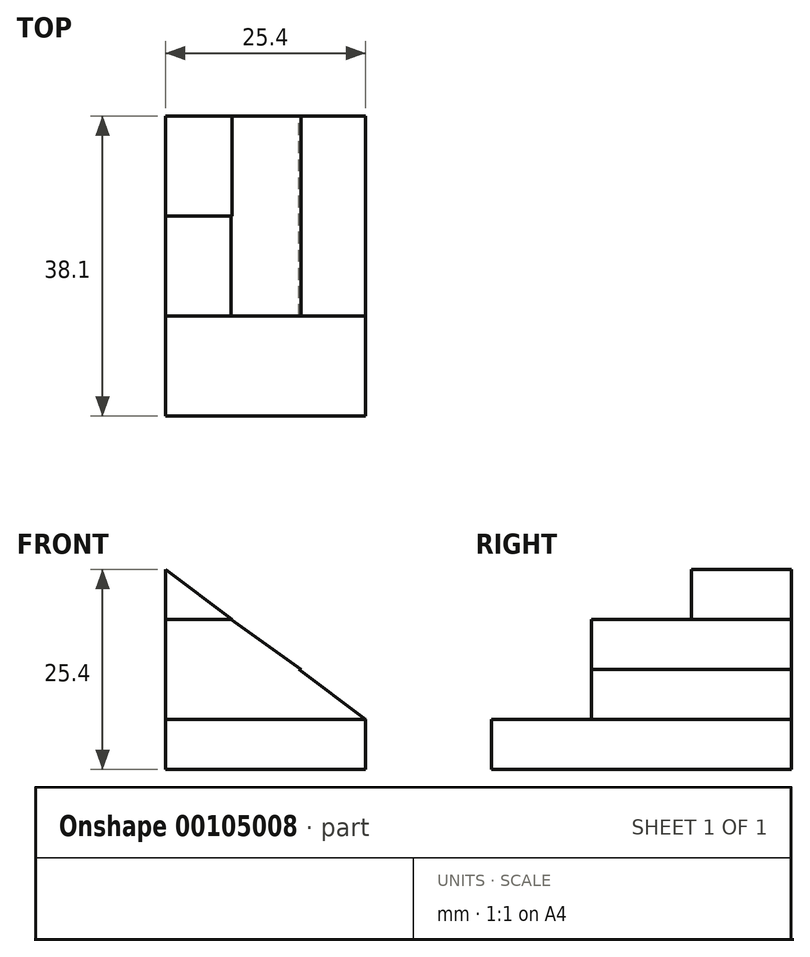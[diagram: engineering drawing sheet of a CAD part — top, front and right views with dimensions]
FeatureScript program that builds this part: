
annotation { "Feature Type Name" : "Feature", "Feature Type Description" : "" }
export const myFeature = defineFeature(function(context is Context, id is Id, definition is map)
    precondition{}
    {
        {
            var Q0;
            Q0=qCreatedBy(makeId("Front.planeOp"),FACE);
            var sketch = newSketch(context, id + "F0", { "sketchPlane" : qUnion([Q0])});
            skLineSegment(sketch, "E0.bottom", {"start": v(0, 0) * mm, "end": v(25.4, 0) * mm});
            skLineSegment(sketch, "E0.top", {"start": v(0, 6.35) * mm, "end": v(25.4, 6.35) * mm});
            skLineSegment(sketch, "E0.left", {"start": v(0, 0) * mm, "end": v(0, 6.35) * mm});
            skLineSegment(sketch, "E0.right", {"start": v(25.4, 0) * mm, "end": v(25.4, 6.35) * mm});
            skLineSegment(sketch, "E1", {"start": v(0, 6.35) * mm, "end": v(0, 25.4) * mm});
            skLineSegment(sketch, "E2", {"start": v(0, 25.4) * mm, "end": v(25.4, 6.35) * mm});
            skLineSegment(sketch, "E3", {"start": v(0, 19.05) * mm, "end": v(8.47, 19.05) * mm});
            skLineSegment(sketch, "E4", {"start": v(8.47, 19.05) * mm, "end": v(19.05, 11.11) * mm});
            skLineSegment(sketch, "E5", {"start": v(19.05, 11.11) * mm, "end": v(19.05, 6.35) * mm});
            skSolve(sketch);
        }
        {
            var Q0;
            Q0=qCreatedBy(makeId("Right.planeOp"),FACE);
            var sketch = newSketch(context, id + "F1", { "sketchPlane" : qUnion([Q0])});
            skLineSegment(sketch, "E6.bottom", {"start": v(0, 0) * mm, "end": v(38.1, 0) * mm});
            skLineSegment(sketch, "E6.top", {"start": v(0, 6.35) * mm, "end": v(38.1, 6.35) * mm});
            skLineSegment(sketch, "E6.left", {"start": v(0, 0) * mm, "end": v(0, 6.35) * mm});
            skLineSegment(sketch, "E6.right", {"start": v(38.1, 0) * mm, "end": v(38.1, 6.35) * mm});
            skLineSegment(sketch, "E7.bottom", {"start": v(25.4, 6.35) * mm, "end": v(12.7, 6.35) * mm});
            skLineSegment(sketch, "E7.top", {"start": v(25.4, 12.7) * mm, "end": v(12.7, 12.7) * mm});
            skLineSegment(sketch, "E7.left", {"start": v(25.4, 6.35) * mm, "end": v(25.4, 12.7) * mm});
            skLineSegment(sketch, "E7.right", {"start": v(12.7, 6.35) * mm, "end": v(12.7, 12.7) * mm});
            skLineSegment(sketch, "E8", {"start": v(12.7, 12.7) * mm, "end": v(12.7, 19.05) * mm});
            skLineSegment(sketch, "E9", {"start": v(12.7, 19.05) * mm, "end": v(25.4, 19.05) * mm});
            skLineSegment(sketch, "E10", {"start": v(25.4, 19.05) * mm, "end": v(25.4, 25.4) * mm});
            skLineSegment(sketch, "E11", {"start": v(25.4, 25.4) * mm, "end": v(38.1, 25.4) * mm});
            skLineSegment(sketch, "E12", {"start": v(38.1, 25.4) * mm, "end": v(38.1, 6.35) * mm});
            skSolve(sketch);
        }
        {
            var Q0;
            Q0=makeQuery(id+"F1.imprint","IMPRINT",FACE,{"disambiguationData":[TD([[makeQuery(id+"F1.imprint","IMPRINT",EDGE,{"derivedFrom":sQuery(id+"F1.wireOp",EDGE,"E6.bottom")}),1.0]])]});
            var Q1;
            Q1=makeQuery(id+"F1.imprint","IMPRINT",FACE,{"disambiguationData":[TD([[makeQuery(id+"F1.imprint","IMPRINT",EDGE,{"derivedFrom":sQuery(id+"F1.wireOp",EDGE,"E7.top")}),-1.0]])]});
            extrude(context, id + "F2", {"entities" : qUnion([Q0, Q1]), "depth" : 25.4 * mm});
        }
        {
            var Q0;
            Q0 = qSketchRegion(id + "F0", true);
            extrude(context, id + "F3", {"entities" : qUnion([Q0]), "operationType" : NewBodyOperationType.ADD, "oppositeDirection" : true, "depth" : 25.4 * mm});
        }
        {
            var Q0;
            Q0=makeQuery(id+"F3.boolean.opBoolean","MERGE",FACE,{"derivedFrom":[makeQuery(id+"F2.opExtrude","SWEPT_FACE",FACE,{"disambiguationData":[OSD([sQuery(id+"F1.wireOp",EDGE,"E6.left")])]}),makeQuery(id+"F3.opExtrude","CAP_FACE",FACE,{"disambiguationData":[OSD([sQuery(id+"F0.wireOp",EDGE,"E0.bottom"),sQuery(id+"F0.wireOp",EDGE,"E0.left"),sQuery(id+"F0.wireOp",EDGE,"E0.right"),sQuery(id+"F0.wireOp",EDGE,"E1"),sQuery(id+"F0.wireOp",EDGE,"E2"),sQuery(id+"F0.wireOp",EDGE,"E4")])],"isStart":true})]});
            var sketch = newSketch(context, id + "F4", { "sketchPlane" : qUnion([Q0])});
            skLineSegment(sketch, "E13", {"start": v(0, 25.4) * mm, "end": v(0, 6.35) * mm});
            skLineSegment(sketch, "E14", {"start": v(0, 6.35) * mm, "end": v(25.4, 6.35) * mm});
            skSolve(sketch);
        }
        {
            var Q0;
            Q0=makeQuery(id+"F4.imprint","IMPRINT",FACE,{"disambiguationData":[TD([[makeQuery(id+"F4.imprint","IMPRINT",EDGE,{"derivedFrom":sQuery(id+"F4.wireOp",EDGE,"E13")}),-1.0]])]});
            extrude(context, id + "F5", {"entities" : qUnion([Q0]), "operationType" : NewBodyOperationType.REMOVE, "oppositeDirection" : true, "depth" : 12.7 * mm});
        }
        {
            var Q0;
            Q0=makeQuery(id+"F5.boolean.opBoolean","MERGE",FACE,{"derivedFrom":[makeQuery(id+"F2.opExtrude","SWEPT_FACE",FACE,{"disambiguationData":[OSD([sQuery(id+"F1.wireOp",EDGE,"E8")])]}),makeQuery(id+"F5.opExtrude","CAP_FACE",FACE,{"disambiguationData":[OSD([sQuery(id+"F0.wireOp",EDGE,"E2"),sQuery(id+"F0.wireOp",EDGE,"E4"),sQuery(id+"F4.wireOp",EDGE,"E13"),sQuery(id+"F4.wireOp",EDGE,"E14")])],"isStart":false})]});
            var sketch = newSketch(context, id + "F6", { "sketchPlane" : qUnion([Q0])});
            skLineSegment(sketch, "E15", {"start": v(8.47, 19.05) * mm, "end": v(0, 19.05) * mm});
            skSolve(sketch);
        }
        {
            var Q0;
            Q0=makeQuery(id+"F2.opExtrude","SWEPT_FACE",FACE,{"disambiguationData":[OSD([sQuery(id+"F1.wireOp",EDGE,"E10")])]});
            extrude(context, id + "F7", {"entities" : qUnion([Q0]), "operationType" : NewBodyOperationType.REMOVE, "oppositeDirection" : true, "depth" : 12.7 * mm});
        }
        {
            var Q0;
            {var subQ2=sQuery(id+"F6.wireOp",EDGE,"E15");Q0=makeQuery(id+"F6.imprint","IMPRINT",FACE,{"disambiguationData":[TD([[makeQuery(id+"F6.imprint","IMPRINT",EDGE,{"derivedFrom":subQ2}),1.0]])]});}
            var sketch = newSketch(context, id + "F8", { "sketchPlane" : qUnion([Q0])});
            skLineSegment(sketch, "E16", {"start": v(8.24, 19.12) * mm, "end": v(17.38, 12.6) * mm});
            skSolve(sketch);
        }
        {
            var Q0;
            {var subQ0=sQuery(id+"F1.wireOp",EDGE,"E8");var subQ6=makeQuery(id+"F6.imprint","IMPRINT",EDGE,{"derivedFrom":makeQuery(id+"F2.opExtrude","CAP_EDGE",EDGE,{"disambiguationData":[OSD([subQ0])],"isStart":false})});Q0=makeQuery(id+"F8.imprint","IMPRINT",FACE,{"disambiguationData":[TD([[makeQuery(id+"F8.imprint","IMPRINT",EDGE,{"derivedFrom":subQ6}),1.0]])]});}
            extrude(context, id + "F9", {"entities" : qUnion([Q0]), "operationType" : NewBodyOperationType.REMOVE, "oppositeDirection" : true, "depth" : 25.4 * mm});
        }
        {
            var Q0;
            {var subQ0=sQuery(id+"F6.wireOp",EDGE,"E15");Q0=makeQuery(id+"F6.imprint","IMPRINT",FACE,{"disambiguationData":[TD([[makeQuery(id+"F6.imprint","IMPRINT",EDGE,{"derivedFrom":subQ0}),-1.0]])]});}
            extrude(context, id + "F10", {"entities" : qUnion([Q0]), "operationType" : NewBodyOperationType.REMOVE, "oppositeDirection" : true, "depth" : 12.7 * mm});
        }
        {
            var Q0;
            Q0=makeQuery(id+"F2.opExtrude","SWEPT_FACE",FACE,{"disambiguationData":[OSD([sQuery(id+"F1.wireOp",EDGE,"E7.left")])]});
            extrude(context, id + "F11", {"entities" : qUnion([Q0]), "operationType" : NewBodyOperationType.REMOVE, "oppositeDirection" : true, "depth" : 12.7 * mm});
        }
    });
